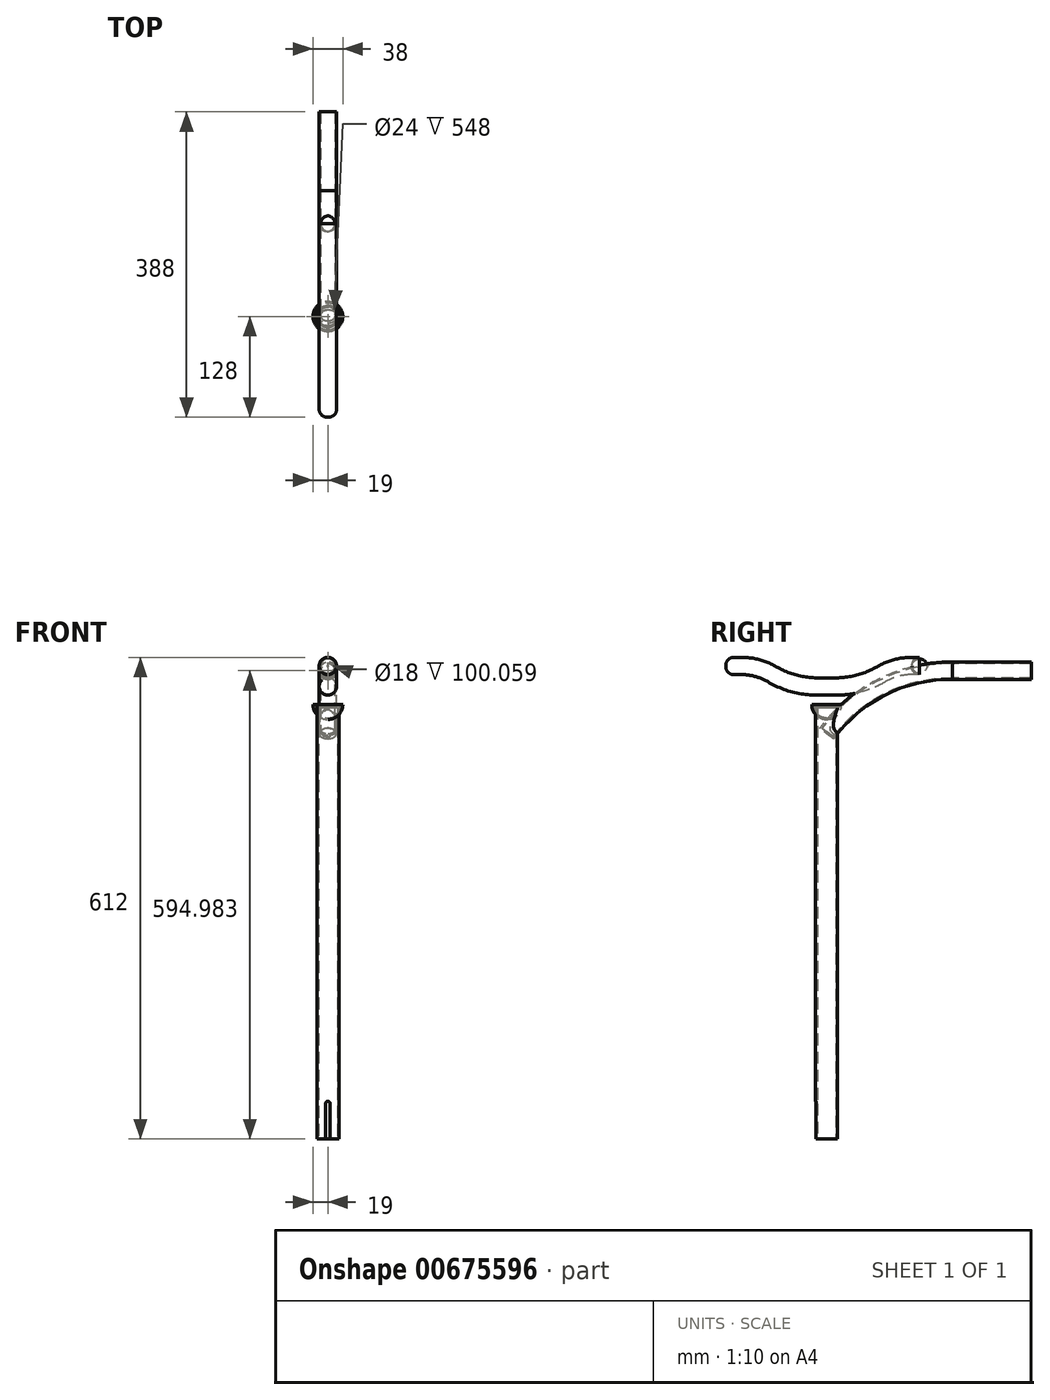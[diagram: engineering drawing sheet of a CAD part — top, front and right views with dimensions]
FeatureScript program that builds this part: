
annotation { "Feature Type Name" : "Feature", "Feature Type Description" : "" }
export const myFeature = defineFeature(function(context is Context, id is Id, definition is map)
    precondition{}
    {
        {
            var Q0;
            Q0=qCreatedBy(makeId("Top.planeOp"),FACE);
            var sketch = newSketch(context, id + "F0", { "sketchPlane" : qUnion([Q0])});
            skCircle(sketch, "E0", {"center": v(0, 0) * mm, "radius": 14 * mm});
            skSolve(sketch);
        }
        {
            var Q0;
            Q0 = qSketchRegion(id + "F0", true);
            extrude(context, id + "F1", {"entities" : qUnion([Q0]), "depth" : 550 * mm, "offsetDistance" : 25 * mm});
        }
        {
            var Q0;
            Q0=makeQuery(id+"F1.opExtrude","CAP_FACE",FACE,{"disambiguationData":[OSD([sQuery(id+"F0.wireOp",EDGE,"E0")])],"isStart":true});
            shell(context, id + "F2", {"entities" : qUnion([Q0]), "thickness" : 2 * mm});
        }
        {
            var Q0;
            Q0=qCreatedBy(makeId("Front.planeOp"),FACE);
            var sketch = newSketch(context, id + "F3", { "sketchPlane" : qUnion([Q0])});
            skLineSegment(sketch, "E1.bottom", {"start": v(-3, 0) * mm, "end": v(3, 0) * mm});
            skLineSegment(sketch, "E1.left", {"start": v(-3, 0) * mm, "end": v(-3, 45) * mm});
            skLineSegment(sketch, "E1.right", {"start": v(3, 0) * mm, "end": v(3, 45) * mm});
            skArc(sketch, "E2", {"start": v(3, 45) * mm, "mid": v(0, 48) * mm, "end": v(-3, 45) * mm});
            skSolve(sketch);
        }
        {
            var Q0;
            Q0 = qSketchRegion(id + "F3", true);
            extrude(context, id + "F4", {"entities" : qUnion([Q0]), "operationType" : NewBodyOperationType.REMOVE, "endBound" : BoundingType.THROUGH_ALL, "depth" : 25 * mm, "offsetDistance" : 25 * mm});
        }
        {
            var Q0;
            Q0=qCreatedBy(makeId("Right.planeOp"),FACE);
            var sketch = newSketch(context, id + "F5", { "sketchPlane" : qUnion([Q0])});
            skArc(sketch, "E3", {"start": v(160, 594.98) * mm, "mid": v(70.3, 574.44) * mm, "end": v(0, 515.04) * mm});
            skLineSegment(sketch, "E4", {"start": v(160, 594.98) * mm, "end": v(260, 594.98) * mm});
            skSolve(sketch);
        }
        {
            var Q0;
            Q0=sQuery(id+"F5.wireOp",VERTEX,"E4.end");
            var Q1;
            Q1=qCreatedBy(makeId("Front.planeOp"),FACE);
            cPlane(context, id + "F6", {"entities" : qUnion([Q0, Q1]), "cplaneType" : CPlaneType.PLANE_POINT, "offset" : 25 * mm, "width" : 150 * mm, "height" : 150 * mm});
        }
        {
            var Q0;
            Q0=qCreatedBy(makeId("Right.planeOp"),FACE);
            var sketch = newSketch(context, id + "F7", { "sketchPlane" : qUnion([Q0])});
            skLineSegment(sketch, "E5", {"start": v(-128, 601) * mm, "end": v(-108, 601) * mm});
            skArc(sketch, "E6", {"start": v(-69.28, 590.46) * mm, "mid": v(-41.92, 578.93) * mm, "end": v(-12.5, 575) * mm});
            skLineSegment(sketch, "E7", {"start": v(-12.5, 575) * mm, "end": v(0, 575) * mm});
            skPoint(sketch, "E8.MirrorCS.end.orphan", {"position": v(0, 575) * mm});
            skPoint(sketch, "E8.MirrorCS.start.orphan", {"position": v(12.5, 575) * mm});
            skPoint(sketch, "E9.MirrorCS.start.orphan", {"position": v(69.28, 590.46) * mm});
            skPoint(sketch, "E10.MirrorCS.end.orphan", {"position": v(108, 601) * mm});
            skPoint(sketch, "E10.MirrorCS.start.orphan", {"position": v(128, 601) * mm});
            skArc(sketch, "E11", {"start": v(-69.28, 590.46) * mm, "mid": v(-87.93, 598.32) * mm, "end": v(-108, 601) * mm});
            skLineSegment(sketch, "E12.MirrorCS", {"start": v(12.5, 575) * mm, "end": v(0, 575) * mm});
            skArc(sketch, "E13.MirrorCS", {"start": v(69.28, 590.46) * mm, "mid": v(41.92, 578.93) * mm, "end": v(12.5, 575) * mm});
            skArc(sketch, "E14.MirrorCS", {"start": v(69.28, 590.46) * mm, "mid": v(87.93, 598.32) * mm, "end": v(108, 601) * mm});
            skLineSegment(sketch, "E15.MirrorCS", {"start": v(128, 601) * mm, "end": v(108, 601) * mm});
            skSolve(sketch);
        }
        {
            var Q0;
            Q0=qCreatedBy(id+"F6.planeOp",FACE);
            var sketch = newSketch(context, id + "F8", { "sketchPlane" : qUnion([Q0])});
            skCircle(sketch, "E16", {"center": v(0, 594.98) * mm, "radius": 11 * mm});
            skSolve(sketch);
        }
        {
            var Q0;
            Q0 = qSketchRegion(id + "F5", true);
            var Q1;
            Q1 = qSketchRegion(id + "F8", true);
            var Q2;
            Q2 = qConstructionFilter(qBodyType(qCreatedBy(id + "F5" ,EDGE), BodyType.WIRE), ConstructionObject.NO);
            sweep(context, id + "F9", {"operationType" : NewBodyOperationType.ADD, "profiles" : qUnion([Q0, Q1]), "path" : qUnion([Q2])});
        }
        {
            var Q0;
            Q0=makeQuery(id+"F9.opSweep","CAP_FACE",FACE,{"disambiguationData":[OSD([sQuery(id+"F5.wireOp",VERTEX,"E4.end"),sQuery(id+"F8.wireOp",EDGE,"E16")])],"isStart":true});
            shell(context, id + "F10", {"entities" : qUnion([Q0]), "thickness" : 2 * mm});
        }
        {
            var Q0;
            Q0=sQuery(id+"F7.wireOp",VERTEX,"E10.MirrorCS.start.orphan");
            var Q1;
            Q1=qCreatedBy(id+"F6.planeOp",FACE);
            cPlane(context, id + "F11", {"entities" : qUnion([Q0, Q1]), "cplaneType" : CPlaneType.PLANE_POINT, "offset" : 25 * mm, "width" : 150 * mm, "height" : 150 * mm});
        }
        {
            var Q0;
            Q0=qCreatedBy(id+"F11.planeOp",FACE);
            var sketch = newSketch(context, id + "F12", { "sketchPlane" : qUnion([Q0])});
            skCircle(sketch, "E17", {"center": v(0, 601) * mm, "radius": 11 * mm});
            skSolve(sketch);
        }
        {
            var Q0;
            Q0 = qSketchRegion(id + "F12", true);
            var Q1;
            Q1 = qConstructionFilter(qBodyType(qCreatedBy(id + "F7" ,EDGE), BodyType.WIRE), ConstructionObject.NO);
            sweep(context, id + "F13", {"profiles" : qUnion([Q0]), "path" : qUnion([Q1])});
        }
        {
            var Q0;
            Q0=makeQuery(id+"F13.opSweep","CAP_EDGE",EDGE,{"disambiguationData":[OSD([sQuery(id+"F7.wireOp",VERTEX,"E15.MirrorCS.start"),sQuery(id+"F12.wireOp",EDGE,"E17")])],"isStart":true});
            var Q1;
            Q1=makeQuery(id+"F13.opSweep","CAP_EDGE",EDGE,{"disambiguationData":[OSD([sQuery(id+"F7.wireOp",VERTEX,"E5.start"),sQuery(id+"F12.wireOp",EDGE,"E17")])],"isStart":false});
            fillet(context, id + "F14", {"entities" : qUnion([Q0, Q1]), "radius" : 10 * mm, "tangentPropagation" : true, "allowEdgeOverflow" : false});
        }
        {
            var Q0;
            Q0=qCreatedBy(makeId("Right.planeOp"),FACE);
            var sketch = newSketch(context, id + "F15", { "sketchPlane" : qUnion([Q0])});
            skArc(sketch, "E18", {"start": v(-19, 551.88) * mm, "mid": v(-13.4, 538.52) * mm, "end": v(0, 533) * mm});
            skLineSegment(sketch, "E19", {"start": v(0, 552) * mm, "end": v(0, 533) * mm});
            skLineSegment(sketch, "E20", {"start": v(-19, 551.88) * mm, "end": v(0, 551.88) * mm});
            skPoint(sketch, "E21.orphan", {"position": v(0, 571) * mm});
            skSolve(sketch);
        }
        {
            var Q0;
            Q0 = qSketchRegion(id + "F15", true);
            var Q1;
            Q1=sQuery(id+"F15.wireOp",EDGE,"E19");
            revolve(context, id + "F16", {"surfaceOperationType" : NewSurfaceOperationType.NEW, "entities" : qUnion([Q0]), "axis" : qUnion([Q1]), "revolveType" : RevolveType.FULL});
        }
        {
            var Q0;
            Q0=makeQuery(id+"F16.opRevolve","SWEPT_FACE",FACE,{"disambiguationData":[OSD([sQuery(id+"F15.wireOp",EDGE,"E20")])]});
            shell(context, id + "F17", {"entities" : qUnion([Q0]), "thickness" : 2 * mm});
        }
    });
